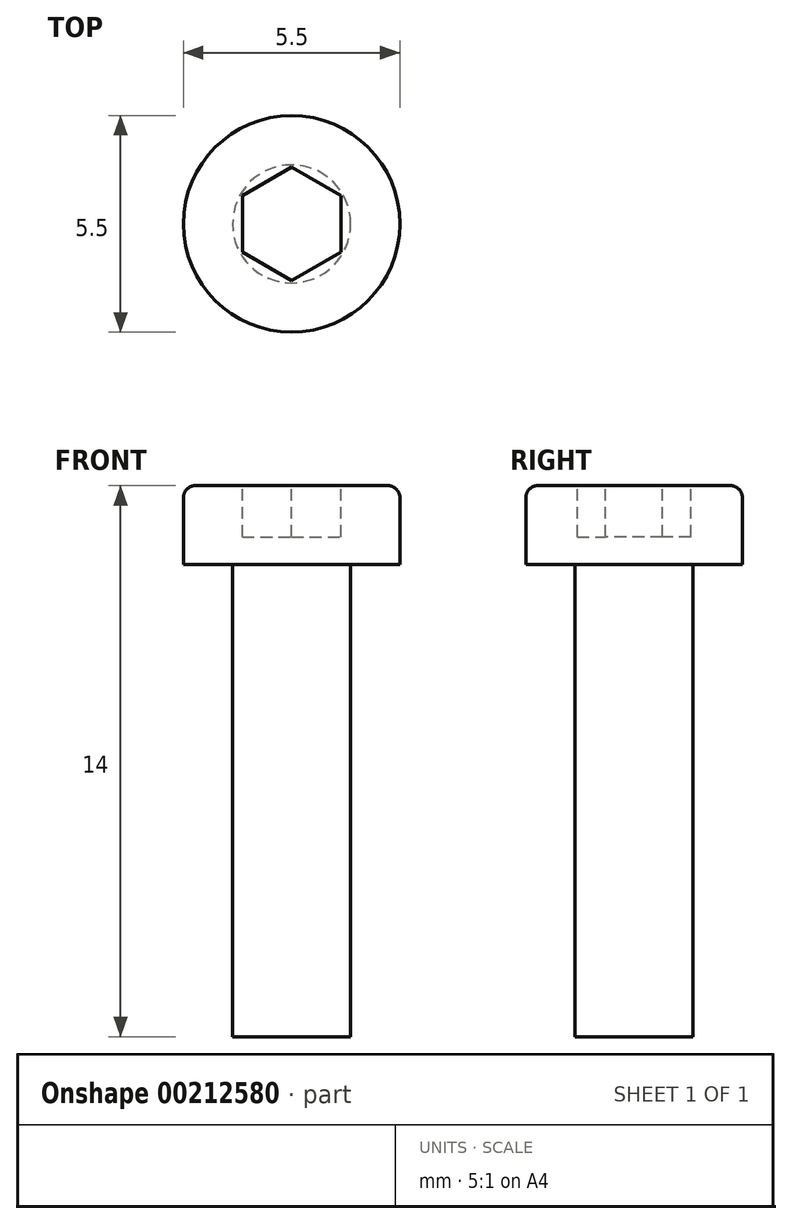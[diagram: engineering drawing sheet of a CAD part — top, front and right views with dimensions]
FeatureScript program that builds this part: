
annotation { "Feature Type Name" : "Feature", "Feature Type Description" : "" }
export const myFeature = defineFeature(function(context is Context, id is Id, definition is map)
    precondition{}
    {
        {
            var Q0;
            Q0=qCreatedBy(makeId("Top.planeOp"),FACE);
            var sketch = newSketch(context, id + "F0", { "sketchPlane" : qUnion([Q0])});
            skCircle(sketch, "E0", {"center": v(0, 0) * mm, "radius": 2.75 * mm});
            skSolve(sketch);
        }
        {
            var Q0;
            Q0=makeQuery(id+"F0.imprint","IMPRINT",FACE,{"disambiguationData":[TD([[makeQuery(id+"F0.imprint","IMPRINT",EDGE,{"derivedFrom":sQuery(id+"F0.wireOp",EDGE,"E0")}),1.0]])]});
            extrude(context, id + "F1", {"entities" : qUnion([Q0]), "depth" : (2) * mm, "offsetDistance" : 25 * mm});
        }
        {
            var Q0;
            Q0=makeQuery(id+"F1.opExtrude","CAP_FACE",FACE,{"disambiguationData":[OSD([sQuery(id+"F0.wireOp",EDGE,"E0")])],"isStart":false});
            var sketch = newSketch(context, id + "F2", { "sketchPlane" : qUnion([Q0])});
            skCircle(sketch, "E1.cCircle", {"center": v(0, 0) * mm, "radius": 1.25 * mm, "construction": true});
            skLineSegment(sketch, "E1.0", {"start": v(1.25, 0.72) * mm, "end": v(1.25, -0.72) * mm});
            skLineSegment(sketch, "E1.1", {"start": v(1.25, -0.72) * mm, "end": v(0, -1.44) * mm});
            skLineSegment(sketch, "E1.2", {"start": v(0, -1.44) * mm, "end": v(-1.25, -0.72) * mm});
            skLineSegment(sketch, "E1.3", {"start": v(-1.25, -0.72) * mm, "end": v(-1.25, 0.72) * mm});
            skLineSegment(sketch, "E1.4", {"start": v(-1.25, 0.72) * mm, "end": v(0, 1.44) * mm});
            skLineSegment(sketch, "E1.5", {"start": v(0, 1.44) * mm, "end": v(1.25, 0.72) * mm});
            skPoint(sketch, "E1.0.midPoint", {"position": v(1.25, 0) * mm});
            skSolve(sketch);
        }
        {
            var Q0;
            Q0=makeQuery(id+"F2.imprint","IMPRINT",FACE,{"disambiguationData":[TD([[makeQuery(id+"F2.imprint","IMPRINT",EDGE,{"derivedFrom":sQuery(id+"F2.wireOp",EDGE,"E1.0")}),-1.0]])]});
            extrude(context, id + "F3", {"entities" : qUnion([Q0]), "operationType" : NewBodyOperationType.REMOVE, "oppositeDirection" : true, "depth" : 1.3 * mm, "offsetDistance" : 25 * mm});
        }
        {
            var Q0;
            Q0=makeQuery(id+"F1.opExtrude","CAP_FACE",FACE,{"disambiguationData":[OSD([sQuery(id+"F0.wireOp",EDGE,"E0")])],"isStart":true});
            var sketch = newSketch(context, id + "F4", { "sketchPlane" : qUnion([Q0])});
            skCircle(sketch, "E2", {"center": v(0, 0) * mm, "radius": 1.5 * mm});
            skSolve(sketch);
        }
        {
            var Q0;
            Q0=makeQuery(id+"F4.imprint","IMPRINT",FACE,{"disambiguationData":[TD([[makeQuery(id+"F4.imprint","IMPRINT",EDGE,{"derivedFrom":sQuery(id+"F4.wireOp",EDGE,"E2")}),1.0]])]});
            extrude(context, id + "F5", {"entities" : qUnion([Q0]), "operationType" : NewBodyOperationType.ADD, "depth" : 12 * mm, "offsetDistance" : 25 * mm});
        }
        {
            var Q0;
            Q0=makeQuery(id+"F1.opExtrude","CAP_EDGE",EDGE,{"disambiguationData":[OSD([sQuery(id+"F0.wireOp",EDGE,"E0")])],"isStart":false});
            fillet(context, id + "F6", {"entities" : qUnion([Q0]), "tangentPropagation" : true, "radius" : 0.3 * mm, "defaultsChanged" : true, "vertexSettings" : [], "allowEdgeOverflow" : false});
        }
    });
